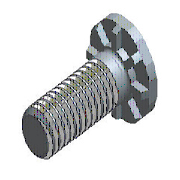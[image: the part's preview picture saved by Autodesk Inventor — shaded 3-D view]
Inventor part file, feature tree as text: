
AUTODESK INVENTOR PART (.ipt)
format: ipt  version: 2024 (Build 280153000, 153)  size: 305,664 bytes
history: native  units: in
note: dims shown in document units (in); Inventor stores cm internally (conversion verified against a paired STEP export)
features: sketch x3, other x2
ambient origin geometry x8: Origin, YZ Plane, XZ Plane, XY Plane, X Axis, Y Axis, Z Axis, Center Point
bodies: Solid1 (feature_tree)
feature tree (5):
  sketch  "Boceto6"  dims[d2=0.048in d3=2.0in d4=0.102in d5=0.034in d6=0.1908in d7=0.206in d8=0.004in d9=90.0deg d10=0.016in d12=0.028in d13=0.595in d14=0.0in d15=0.012in d16=0.125in d17=45.0deg d18=0.357in d19=0.0315in d20=1.0in d21=0.0in d22=3.1496in d23=360.0deg d25=0.357in d26=0.1374in d27=90.0deg d28=0.357in d29=1.0in d30=0.0in d31=3.1496in d32=360.0deg d34=0.0in d35=0.0in d36=0.0in d37=2.624in d38=0.3937in d39=0.3937in]
  other  "Edición directa1"
  sketch  "Sketch3"  dims[d0=0.19in]
  sketch  "Sketch4"  dims[d1=0.3677in]
  other  "Escala1"
